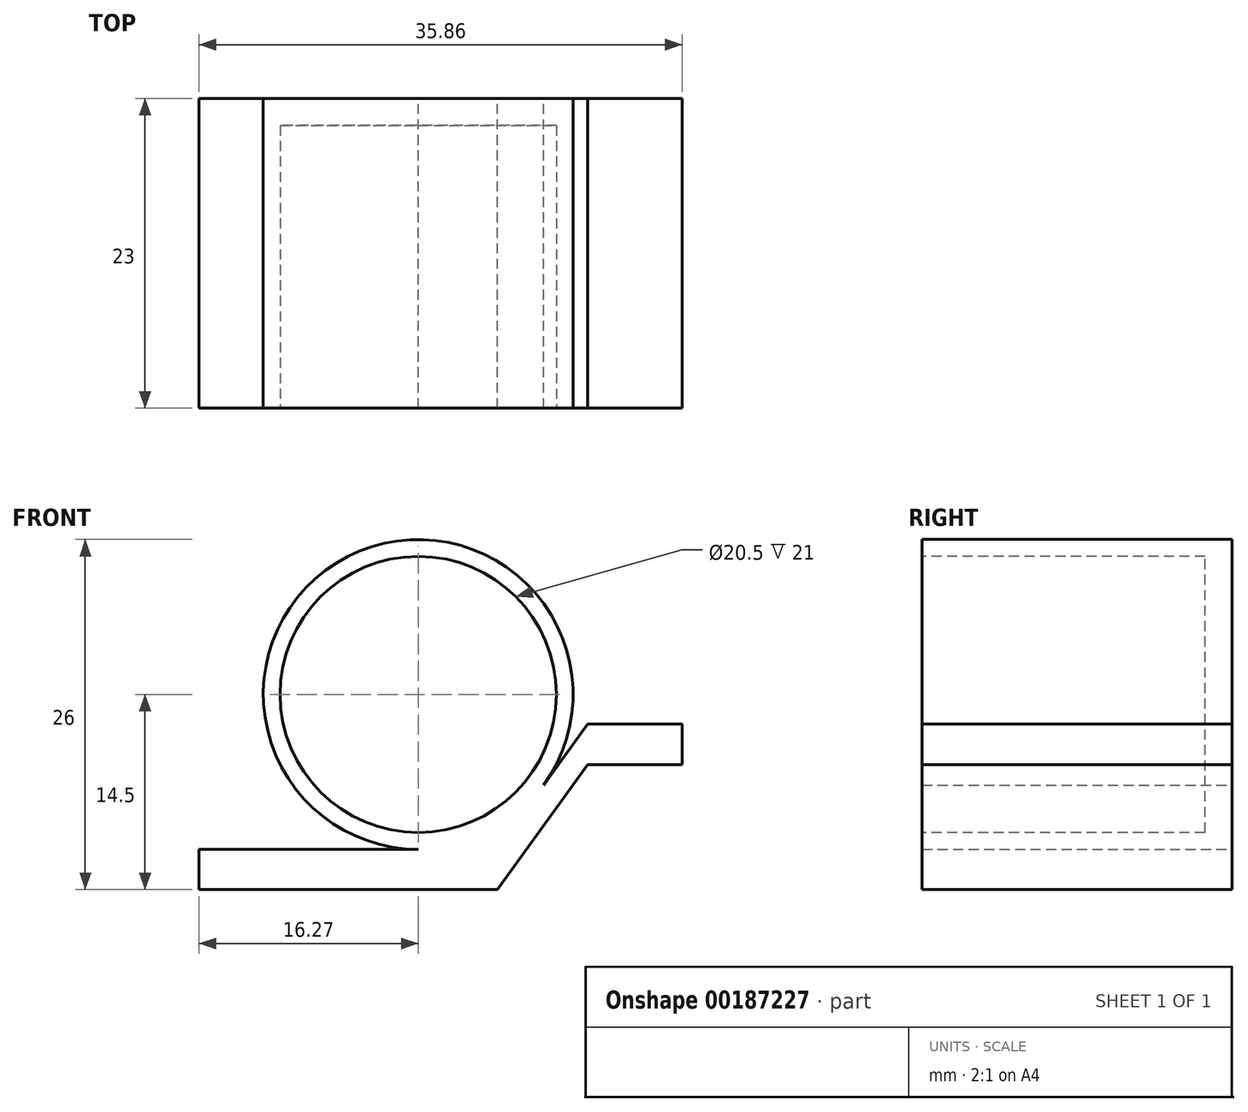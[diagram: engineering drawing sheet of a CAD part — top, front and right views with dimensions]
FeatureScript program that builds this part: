
annotation { "Feature Type Name" : "Feature", "Feature Type Description" : "" }
export const myFeature = defineFeature(function(context is Context, id is Id, definition is map)
    precondition{}
    {
        {
            var Q0;
            Q0=qCreatedBy(makeId("Front.planeOp"),FACE);
            var sketch = newSketch(context, id + "F0", { "sketchPlane" : qUnion([Q0])});
            skCircle(sketch, "E0", {"center": v(0, 0) * mm, "radius": 11.5 * mm});
            skLineSegment(sketch, "E1.bottom", {"start": v(-16.27, -14.5) * mm, "end": v(5.88, -14.5) * mm});
            skLineSegment(sketch, "E1.top", {"start": v(-16.27, -11.5) * mm, "end": v(5.88, -11.5) * mm});
            skLineSegment(sketch, "E1.left", {"start": v(-16.27, -11.5) * mm, "end": v(-16.27, -14.5) * mm});
            skLineSegment(sketch, "E1.right", {"start": v(5.88, -11.5) * mm, "end": v(5.88, -14.5) * mm});
            skLineSegment(sketch, "E2.bottom", {"start": v(-16.27, -14.5) * mm, "end": v(-16.27, -14.5) * mm});
            skLineSegment(sketch, "E2.top", {"start": v(-16.27, -11.5) * mm, "end": v(-16.27, -11.5) * mm});
            skLineSegment(sketch, "E3.bottom", {"start": v(12.6, -5.2) * mm, "end": v(19.6, -5.2) * mm});
            skLineSegment(sketch, "E3.top", {"start": v(12.6, -2.2) * mm, "end": v(19.6, -2.2) * mm});
            skLineSegment(sketch, "E3.left", {"start": v(12.6, -2.2) * mm, "end": v(12.6, -5.2) * mm});
            skLineSegment(sketch, "E3.right", {"start": v(19.6, -2.2) * mm, "end": v(19.6, -5.2) * mm});
            skLineSegment(sketch, "E4.bottom", {"start": v(12.6, -5.2) * mm, "end": v(12.6, -5.2) * mm});
            skLineSegment(sketch, "E4.top", {"start": v(12.6, -2.2) * mm, "end": v(12.6, -2.2) * mm});
            skLineSegment(sketch, "E5", {"start": v(5.88, -11.5) * mm, "end": v(12.6, -2.2) * mm});
            skLineSegment(sketch, "E6", {"start": v(12.6, -5.2) * mm, "end": v(5.88, -14.5) * mm});
            skSolve(sketch);
        }
        {
            var Q0;
            Q0 = qSketchRegion(id + "F0", true);
            extrude(context, id + "F1", {"entities" : qUnion([Q0]), "depth" : 23 * mm});
        }
        {
            var Q0;
            Q0=makeQuery(id+"F1.opExtrude","CAP_FACE",FACE,{"disambiguationData":[OSD([sQuery(id+"F0.wireOp",EDGE,"E0"),sQuery(id+"F0.wireOp",EDGE,"E1.bottom"),sQuery(id+"F0.wireOp",EDGE,"E1.top"),sQuery(id+"F0.wireOp",EDGE,"E1.left"),sQuery(id+"F0.wireOp",EDGE,"E3.bottom"),sQuery(id+"F0.wireOp",EDGE,"E3.top"),sQuery(id+"F0.wireOp",EDGE,"E3.right"),sQuery(id+"F0.wireOp",EDGE,"E5"),sQuery(id+"F0.wireOp",EDGE,"E6")])],"isStart":false});
            var sketch = newSketch(context, id + "F2", { "sketchPlane" : qUnion([Q0])});
            skCircle(sketch, "E7", {"center": v(0, 0) * mm, "radius": 10.25 * mm});
            skSolve(sketch);
        }
        {
            var Q0;
            Q0 = qSketchRegion(id + "F2", true);
            extrude(context, id + "F3", {"entities" : qUnion([Q0]), "operationType" : NewBodyOperationType.REMOVE, "oppositeDirection" : true, "depth" : 21 * mm});
        }
    });
